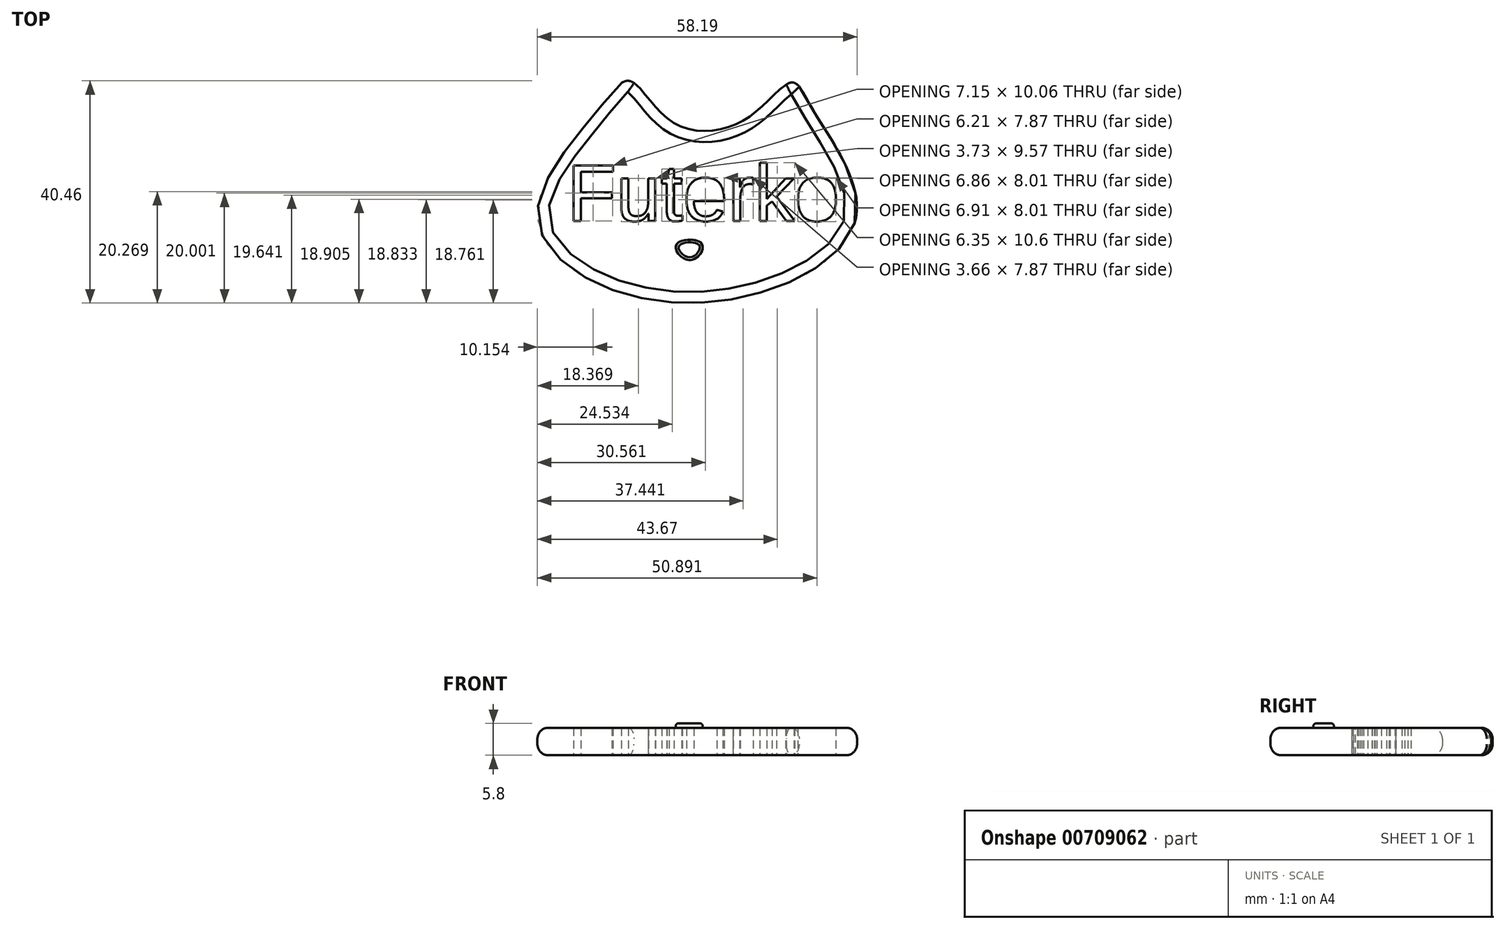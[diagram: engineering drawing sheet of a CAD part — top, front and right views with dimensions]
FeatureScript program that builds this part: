
annotation { "Feature Type Name" : "Feature", "Feature Type Description" : "" }
export const myFeature = defineFeature(function(context is Context, id is Id, definition is map)
    precondition{}
    {
        {
            var Q0;
            Q0=qCreatedBy(makeId("Top.planeOp"),FACE);
            var sketch = newSketch(context, id + "F0", { "sketchPlane" : qUnion([Q0])});
            skText(sketch, "E0", { "text": "Futerko\n", "fontName": "Arimo-Regular.ttf"});
            skFitSpline(sketch, "E1", {"points": [v(8.77, 25.43) * mm, v(2.81, 20.1) * mm, v(-8.05, 0) * mm, v(18.04, -14.94) * mm, v(49.75, 0) * mm, v(42.04, 20.16) * mm, v(38.12, 25.2) * mm, v(29.87, 18.55) * mm, v(16.28, 18.07) * mm, v(8.77, 25.43) * mm]});
            const initialGuessF0  = {"E0": [-0.00275, 0, 1, 0, 0.01053]};
            skSetInitialGuess(sketch, initialGuessF0);
            skSolve(sketch);
        }
        {
            var Q0;
            Q0=makeQuery(id+"F0.imprint","IMPRINT",FACE,{"disambiguationData":[TD([[makeQuery(id+"F0.imprint","IMPRINT",EDGE,{"derivedFrom":sQuery(id+"F0.wireOp",EDGE,"E0.sketch_text.stroke-0")}),1.0]])]});
            extrude(context, id + "F1", {"entities" : qUnion([Q0]), "depth" : 5 * mm, "offsetDistance" : 25 * mm});
        }
        {
            var Q0;
            Q0=makeQuery(id+"F1.opExtrude","CAP_EDGE",EDGE,{"disambiguationData":[OSD([sQuery(id+"F0.wireOp",EDGE,"E1")])],"isStart":false});
            var Q1;
            Q1=makeQuery(id+"F1.opExtrude","CAP_EDGE",EDGE,{"disambiguationData":[OSD([sQuery(id+"F0.wireOp",EDGE,"E1")])],"isStart":true});
            fillet(context, id + "F2", {"entities" : qUnion([Q0, Q1]), "radius" : 2 * mm, "tangentPropagation" : true, "allowEdgeOverflow" : false});
        }
        {
            var Q0;
            Q0=makeQuery(id+"F1.opExtrude","CAP_FACE",FACE,{"disambiguationData":[OSD([sQuery(id+"F0.wireOp",EDGE,"E0.sketch_text.stroke-0"),sQuery(id+"F0.wireOp",EDGE,"E0.sketch_text.stroke-1"),sQuery(id+"F0.wireOp",EDGE,"E0.sketch_text.stroke-2"),sQuery(id+"F0.wireOp",EDGE,"E0.sketch_text.stroke-3"),sQuery(id+"F0.wireOp",EDGE,"E0.sketch_text.stroke-4"),sQuery(id+"F0.wireOp",EDGE,"E0.sketch_text.stroke-5"),sQuery(id+"F0.wireOp",EDGE,"E0.sketch_text.stroke-6"),sQuery(id+"F0.wireOp",EDGE,"E0.sketch_text.stroke-7"),sQuery(id+"F0.wireOp",EDGE,"E0.sketch_text.stroke-8"),sQuery(id+"F0.wireOp",EDGE,"E0.sketch_text.stroke-9"),sQuery(id+"F0.wireOp",EDGE,"E0.sketch_text.stroke-10"),sQuery(id+"F0.wireOp",EDGE,"E0.sketch_text.stroke-11"),sQuery(id+"F0.wireOp",EDGE,"E0.sketch_text.stroke-12"),sQuery(id+"F0.wireOp",EDGE,"E0.sketch_text.stroke-13"),sQuery(id+"F0.wireOp",EDGE,"E0.sketch_text.stroke-14"),sQuery(id+"F0.wireOp",EDGE,"E0.sketch_text.stroke-15"),sQuery(id+"F0.wireOp",EDGE,"E0.sketch_text.stroke-16"),sQuery(id+"F0.wireOp",EDGE,"E0.sketch_text.stroke-17"),sQuery(id+"F0.wireOp",EDGE,"E0.sketch_text.stroke-18"),sQuery(id+"F0.wireOp",EDGE,"E0.sketch_text.stroke-19"),sQuery(id+"F0.wireOp",EDGE,"E0.sketch_text.stroke-20"),sQuery(id+"F0.wireOp",EDGE,"E0.sketch_text.stroke-21"),sQuery(id+"F0.wireOp",EDGE,"E0.sketch_text.stroke-22"),sQuery(id+"F0.wireOp",EDGE,"E0.sketch_text.stroke-23"),sQuery(id+"F0.wireOp",EDGE,"E0.sketch_text.stroke-24"),sQuery(id+"F0.wireOp",EDGE,"E0.sketch_text.stroke-25"),sQuery(id+"F0.wireOp",EDGE,"E0.sketch_text.stroke-26"),sQuery(id+"F0.wireOp",EDGE,"E0.sketch_text.stroke-27"),sQuery(id+"F0.wireOp",EDGE,"E0.sketch_text.stroke-28"),sQuery(id+"F0.wireOp",EDGE,"E0.sketch_text.stroke-29"),sQuery(id+"F0.wireOp",EDGE,"E0.sketch_text.stroke-30"),sQuery(id+"F0.wireOp",EDGE,"E0.sketch_text.stroke-31"),sQuery(id+"F0.wireOp",EDGE,"E0.sketch_text.stroke-32"),sQuery(id+"F0.wireOp",EDGE,"E0.sketch_text.stroke-33"),sQuery(id+"F0.wireOp",EDGE,"E0.sketch_text.stroke-34"),sQuery(id+"F0.wireOp",EDGE,"E0.sketch_text.stroke-35"),sQuery(id+"F0.wireOp",EDGE,"E0.sketch_text.stroke-36"),sQuery(id+"F0.wireOp",EDGE,"E0.sketch_text.stroke-37"),sQuery(id+"F0.wireOp",EDGE,"E0.sketch_text.stroke-38"),sQuery(id+"F0.wireOp",EDGE,"E0.sketch_text.stroke-39"),sQuery(id+"F0.wireOp",EDGE,"E0.sketch_text.stroke-40"),sQuery(id+"F0.wireOp",EDGE,"E0.sketch_text.stroke-41"),sQuery(id+"F0.wireOp",EDGE,"E0.sketch_text.stroke-42"),sQuery(id+"F0.wireOp",EDGE,"E0.sketch_text.stroke-43"),sQuery(id+"F0.wireOp",EDGE,"E0.sketch_text.stroke-44"),sQuery(id+"F0.wireOp",EDGE,"E0.sketch_text.stroke-45"),sQuery(id+"F0.wireOp",EDGE,"E0.sketch_text.stroke-46"),sQuery(id+"F0.wireOp",EDGE,"E0.sketch_text.stroke-47"),sQuery(id+"F0.wireOp",EDGE,"E0.sketch_text.stroke-48"),sQuery(id+"F0.wireOp",EDGE,"E0.sketch_text.stroke-49"),sQuery(id+"F0.wireOp",EDGE,"E0.sketch_text.stroke-50"),sQuery(id+"F0.wireOp",EDGE,"E0.sketch_text.stroke-51"),sQuery(id+"F0.wireOp",EDGE,"E0.sketch_text.stroke-52"),sQuery(id+"F0.wireOp",EDGE,"E0.sketch_text.stroke-53"),sQuery(id+"F0.wireOp",EDGE,"E0.sketch_text.stroke-54"),sQuery(id+"F0.wireOp",EDGE,"E0.sketch_text.stroke-55"),sQuery(id+"F0.wireOp",EDGE,"E0.sketch_text.stroke-56"),sQuery(id+"F0.wireOp",EDGE,"E0.sketch_text.stroke-57"),sQuery(id+"F0.wireOp",EDGE,"E0.sketch_text.stroke-58"),sQuery(id+"F0.wireOp",EDGE,"E0.sketch_text.stroke-59"),sQuery(id+"F0.wireOp",EDGE,"E0.sketch_text.stroke-60"),sQuery(id+"F0.wireOp",EDGE,"E0.sketch_text.stroke-66"),sQuery(id+"F0.wireOp",EDGE,"E0.sketch_text.stroke-67"),sQuery(id+"F0.wireOp",EDGE,"E0.sketch_text.stroke-68"),sQuery(id+"F0.wireOp",EDGE,"E0.sketch_text.stroke-69"),sQuery(id+"F0.wireOp",EDGE,"E0.sketch_text.stroke-70"),sQuery(id+"F0.wireOp",EDGE,"E0.sketch_text.stroke-71"),sQuery(id+"F0.wireOp",EDGE,"E0.sketch_text.stroke-72"),sQuery(id+"F0.wireOp",EDGE,"E0.sketch_text.stroke-73"),sQuery(id+"F0.wireOp",EDGE,"E0.sketch_text.stroke-74"),sQuery(id+"F0.wireOp",EDGE,"E0.sketch_text.stroke-75"),sQuery(id+"F0.wireOp",EDGE,"E0.sketch_text.stroke-76"),sQuery(id+"F0.wireOp",EDGE,"E0.sketch_text.stroke-77"),sQuery(id+"F0.wireOp",EDGE,"E0.sketch_text.stroke-78"),sQuery(id+"F0.wireOp",EDGE,"E0.sketch_text.stroke-79"),sQuery(id+"F0.wireOp",EDGE,"E0.sketch_text.stroke-80"),sQuery(id+"F0.wireOp",EDGE,"E0.sketch_text.stroke-81"),sQuery(id+"F0.wireOp",EDGE,"E0.sketch_text.stroke-82"),sQuery(id+"F0.wireOp",EDGE,"E0.sketch_text.stroke-83"),sQuery(id+"F0.wireOp",EDGE,"E0.sketch_text.stroke-84"),sQuery(id+"F0.wireOp",EDGE,"E0.sketch_text.stroke-85"),sQuery(id+"F0.wireOp",EDGE,"E0.sketch_text.stroke-86"),sQuery(id+"F0.wireOp",EDGE,"E0.sketch_text.stroke-87"),sQuery(id+"F0.wireOp",EDGE,"E0.sketch_text.stroke-88"),sQuery(id+"F0.wireOp",EDGE,"E0.sketch_text.stroke-89"),sQuery(id+"F0.wireOp",EDGE,"E0.sketch_text.stroke-90"),sQuery(id+"F0.wireOp",EDGE,"E0.sketch_text.stroke-91"),sQuery(id+"F0.wireOp",EDGE,"E0.sketch_text.stroke-92"),sQuery(id+"F0.wireOp",EDGE,"E0.sketch_text.stroke-93"),sQuery(id+"F0.wireOp",EDGE,"E0.sketch_text.stroke-94"),sQuery(id+"F0.wireOp",EDGE,"E0.sketch_text.stroke-95"),sQuery(id+"F0.wireOp",EDGE,"E0.sketch_text.stroke-96"),sQuery(id+"F0.wireOp",EDGE,"E0.sketch_text.stroke-97"),sQuery(id+"F0.wireOp",EDGE,"E0.sketch_text.stroke-98"),sQuery(id+"F0.wireOp",EDGE,"E1")])],"isStart":false});
            var sketch = newSketch(context, id + "F3", { "sketchPlane" : qUnion([Q0])});
            skFitSpline(sketch, "E2", {"points": [v(17.16, -4.34) * mm, v(21.8, -4.18) * mm, v(19.69, -7.15) * mm, v(17.16, -4.34) * mm]});
            skSolve(sketch);
        }
        {
            var Q0;
            Q0 = qSketchRegion(id + "F3", true);
            extrude(context, id + "F4", {"entities" : qUnion([Q0]), "operationType" : NewBodyOperationType.ADD, "depth" : 0.8 * mm, "offsetDistance" : 25 * mm});
        }
        {
            var Q0;
            Q0=makeQuery(id+"F4.opExtrude","CAP_EDGE",EDGE,{"disambiguationData":[OSD([sQuery(id+"F3.wireOp",EDGE,"E2")])],"isStart":false});
            fillet(context, id + "F5", {"entities" : qUnion([Q0]), "radius" : 0.5 * mm, "tangentPropagation" : true, "allowEdgeOverflow" : false});
        }
    });
